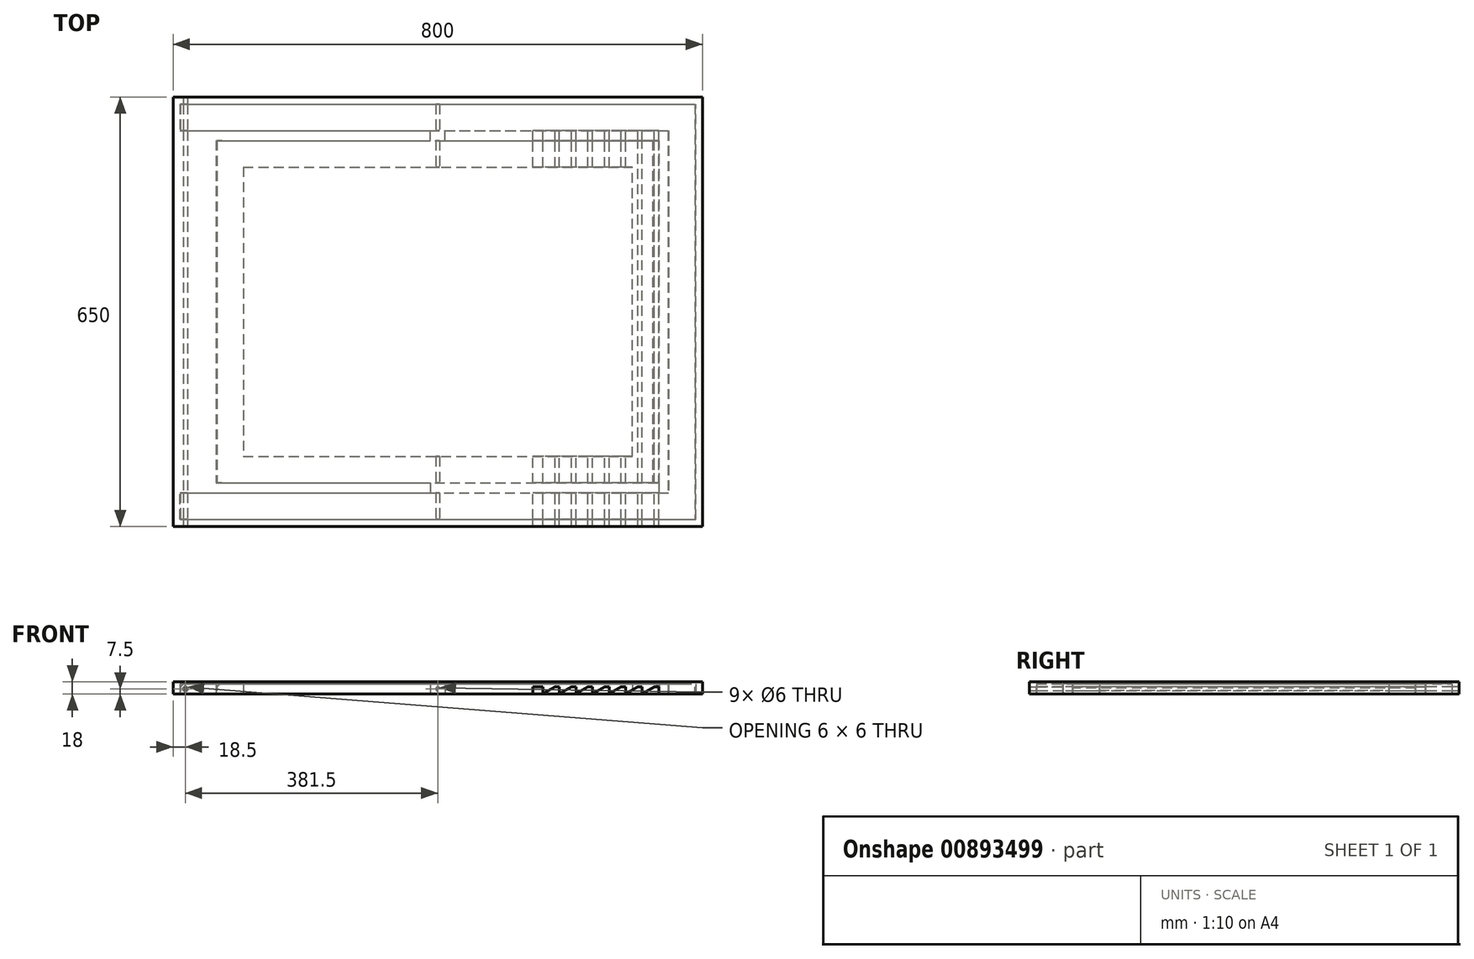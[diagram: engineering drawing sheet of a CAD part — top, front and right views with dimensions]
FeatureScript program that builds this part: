
annotation { "Feature Type Name" : "Feature", "Feature Type Description" : "" }
export const myFeature = defineFeature(function(context is Context, id is Id, definition is map)
    precondition{}
    {
        {
            assignVariable(context, id + "F0", {"name" : "leg_height", "anyValue" : 15});
        }
        {
            assignVariable(context, id + "F1", {"name" : "board_height", "anyValue" : 18});
        }
        {
            var Q0;
            Q0=qCreatedBy(makeId("Top.planeOp"),FACE);
            var sketch = newSketch(context, id + "F2", { "sketchPlane" : qUnion([Q0])});
            skLineSegment(sketch, "E0.bottom", {"start": v(400, -325) * mm, "end": v(-400, -325) * mm});
            skLineSegment(sketch, "E0.top", {"start": v(400, 325) * mm, "end": v(-400, 325) * mm});
            skLineSegment(sketch, "E0.left", {"start": v(400, -325) * mm, "end": v(400, 325) * mm});
            skLineSegment(sketch, "E0.right", {"start": v(-400, -325) * mm, "end": v(-400, 325) * mm});
            skPoint(sketch, "E0.middle", {"position": v(0, 0) * mm});
            skLineSegment(sketch, "E1", {"start": v(-389, 314) * mm, "end": v(389, 314) * mm});
            skLineSegment(sketch, "E2", {"start": v(389, 314) * mm, "end": v(389, 0) * mm});
            skLineSegment(sketch, "E3", {"start": v(-400, 0) * mm, "end": v(-334, 0) * mm, "construction": true});
            skLineSegment(sketch, "E4", {"start": v(-389, 274) * mm, "end": v(349, 274) * mm});
            skLineSegment(sketch, "E5", {"start": v(349, 274) * mm, "end": v(349, 0) * mm});
            skLineSegment(sketch, "E6", {"start": v(-389, 314) * mm, "end": v(-389, 274) * mm});
            skLineSegment(sketch, "E7", {"start": v(349, 0) * mm, "end": v(389, 0) * mm, "construction": true});
            skLineSegment(sketch, "E8", {"start": v(389, 0) * mm, "end": v(400, 0) * mm, "construction": true});
            skLineSegment(sketch, "E9", {"start": v(-334, 259) * mm, "end": v(334, 259) * mm});
            skLineSegment(sketch, "E10", {"start": v(334, 259) * mm, "end": v(334, 0) * mm});
            skLineSegment(sketch, "E11", {"start": v(-334, 259) * mm, "end": v(-334, 0) * mm});
            skLineSegment(sketch, "E12", {"start": v(-294, 0) * mm, "end": v(-294, 219) * mm});
            skLineSegment(sketch, "E13", {"start": v(-294, 219) * mm, "end": v(294, 219) * mm});
            skLineSegment(sketch, "E14", {"start": v(294, 219) * mm, "end": v(294, 0) * mm});
            skLineSegment(sketch, "E15", {"start": v(-334, 0) * mm, "end": v(-294, 0) * mm, "construction": true});
            skLineSegment(sketch, "E16", {"start": v(-294, 0) * mm, "end": v(294, 0) * mm, "construction": true});
            skLineSegment(sketch, "E17", {"start": v(294, 0) * mm, "end": v(334, 0) * mm, "construction": true});
            skLineSegment(sketch, "E18", {"start": v(334, 0) * mm, "end": v(334, 0) * mm});
            skLineSegment(sketch, "E19", {"start": v(349, 0) * mm, "end": v(349, 0) * mm});
            skLineSegment(sketch, "E20", {"start": v(334, 0) * mm, "end": v(349, 0) * mm, "construction": true});
            skLineSegment(sketch, "E21.MirrorCS", {"start": v(-294, 0) * mm, "end": v(-294, -219) * mm});
            skLineSegment(sketch, "E22.MirrorCS", {"start": v(-334, -259) * mm, "end": v(-334, 0) * mm});
            skLineSegment(sketch, "E23.MirrorCS", {"start": v(-334, -259) * mm, "end": v(334, -259) * mm});
            skLineSegment(sketch, "E24.MirrorCS", {"start": v(334, -259) * mm, "end": v(334, 0) * mm});
            skLineSegment(sketch, "E25.MirrorCS", {"start": v(294, -219) * mm, "end": v(294, 0) * mm});
            skLineSegment(sketch, "E26.MirrorCS", {"start": v(-294, -219) * mm, "end": v(294, -219) * mm});
            skLineSegment(sketch, "E27.MirrorCS", {"start": v(-389, -314) * mm, "end": v(-389, -274) * mm});
            skLineSegment(sketch, "E28.MirrorCS", {"start": v(-389, -274) * mm, "end": v(349, -274) * mm});
            skLineSegment(sketch, "E29.MirrorCS", {"start": v(-389, -314) * mm, "end": v(389, -314) * mm});
            skLineSegment(sketch, "E30.MirrorCS", {"start": v(349, -274) * mm, "end": v(349, 0) * mm});
            skLineSegment(sketch, "E31.MirrorCS", {"start": v(389, -314) * mm, "end": v(389, 0) * mm});
            skLineSegment(sketch, "E32", {"start": v(0, 325) * mm, "end": v(0, -325) * mm, "construction": true});
            skLineSegment(sketch, "E33", {"start": v(-11, 259) * mm, "end": v(-11, 274) * mm});
            skLineSegment(sketch, "E34.MirrorCS", {"start": v(11, 259) * mm, "end": v(11, 274) * mm});
            skLineSegment(sketch, "E35.MirrorCS", {"start": v(-11, -259) * mm, "end": v(-11, -274) * mm});
            skLineSegment(sketch, "E36.MirrorCS", {"start": v(11, -259) * mm, "end": v(11, -274) * mm});
            skLineSegment(sketch, "E37", {"start": v(334, -259) * mm, "end": v(334, -274) * mm});
            skLineSegment(sketch, "E38", {"start": v(334, 259) * mm, "end": v(334, 274) * mm});
            skSolve(sketch);
        }
        {
            var Q0;
            Q0 = qSketchRegion(id + "F2", true);
            var Q1;
            Q1=makeQuery(id+"F2.imprint","IMPRINT",FACE,{"disambiguationData":[TD([[makeQuery(id+"F2.imprint","IMPRINT",EDGE,{"derivedFrom":sQuery(id+"F2.wireOp",EDGE,"E1")}),-1.0]])]});
            var Q2;
            Q2=makeQuery(id+"F2.imprint","IMPRINT",FACE,{"disambiguationData":[TD([[makeQuery(id+"F2.imprint","IMPRINT",EDGE,{"derivedFrom":sQuery(id+"F2.wireOp",EDGE,"E12")}),-1.0]])]});
            var Q3;
            Q3=makeQuery(id+"F2.imprint","IMPRINT",FACE,{"disambiguationData":[TD([[makeQuery(id+"F2.imprint","IMPRINT",EDGE,{"derivedFrom":sQuery(id+"F2.wireOp",EDGE,"E9")}),-1.0]])]});
            var Q4;
            {var subQ1=sQuery(id+"F2.wireOp",EDGE,"E5");Q4=makeQuery(id+"F2.imprint","IMPRINT",FACE,{"disambiguationData":[TD([[makeQuery(id+"F2.imprint","IMPRINT",EDGE,{"derivedFrom":subQ1}),-1.0]])]});}
            var Q5;
            {var subQ0=sQuery(id+"F2.wireOp",EDGE,"E35.MirrorCS");Q5=makeQuery(id+"F2.imprint","IMPRINT",FACE,{"disambiguationData":[TD([[makeQuery(id+"F2.imprint","IMPRINT",EDGE,{"derivedFrom":subQ0}),1.0]])]});}
            var Q6;
            {var subQ0=sQuery(id+"F2.wireOp",EDGE,"E33");Q6=makeQuery(id+"F2.imprint","IMPRINT",FACE,{"disambiguationData":[TD([[makeQuery(id+"F2.imprint","IMPRINT",EDGE,{"derivedFrom":subQ0}),-1.0]])]});}
            var Q7;
            {var subQ2=sQuery(id+"F2.wireOp",EDGE,"E36.MirrorCS");Q7=makeQuery(id+"F2.imprint","IMPRINT",FACE,{"disambiguationData":[TD([[makeQuery(id+"F2.imprint","IMPRINT",EDGE,{"derivedFrom":subQ2}),1.0]])]});}
            var Q8;
            {var subQ0=sQuery(id+"F2.wireOp",EDGE,"E34.MirrorCS");Q8=makeQuery(id+"F2.imprint","IMPRINT",FACE,{"disambiguationData":[TD([[makeQuery(id+"F2.imprint","IMPRINT",EDGE,{"derivedFrom":subQ0}),-1.0]])]});}
            extrude(context, id + "F3", {"entities" : qUnion([Q0, Q1, Q2, Q3, Q4, Q5, Q6, Q7, Q8]), "depth" : (getVariable(context, 'board_height')) * mm, "offsetDistance" : 25 * mm});
        }
        {
            var Q0;
            Q0=makeQuery(id+"F2.imprint","IMPRINT",FACE,{"disambiguationData":[TD([[makeQuery(id+"F2.imprint","IMPRINT",EDGE,{"derivedFrom":sQuery(id+"F2.wireOp",EDGE,"E9")}),-1.0]])]});
            var Q1;
            Q1=makeQuery(id+"F2.imprint","IMPRINT",FACE,{"disambiguationData":[TD([[makeQuery(id+"F2.imprint","IMPRINT",EDGE,{"derivedFrom":sQuery(id+"F2.wireOp",EDGE,"E1")}),-1.0]])]});
            extrude(context, id + "F4", {"entities" : qUnion([Q0, Q1]), "depth" : (getVariable(context, 'leg_height')) * mm, "offsetDistance" : 25 * mm});
        }
        {
            var Q0;
            Q0=makeQuery(id+"F4.opExtrude","SWEPT_BODY",BODY,{"disambiguationData":[OSD([sQuery(id+"F2.wireOp",EDGE,"E1"),sQuery(id+"F2.wireOp",EDGE,"E2"),sQuery(id+"F2.wireOp",EDGE,"E4"),sQuery(id+"F2.wireOp",EDGE,"E5"),sQuery(id+"F2.wireOp",EDGE,"E6"),sQuery(id+"F2.wireOp",EDGE,"E27.MirrorCS"),sQuery(id+"F2.wireOp",EDGE,"E28.MirrorCS"),sQuery(id+"F2.wireOp",EDGE,"E29.MirrorCS"),sQuery(id+"F2.wireOp",EDGE,"E30.MirrorCS"),sQuery(id+"F2.wireOp",EDGE,"E31.MirrorCS")])]});
            var Q1;
            Q1=makeQuery(id+"F4.opExtrude","SWEPT_BODY",BODY,{"disambiguationData":[OSD([sQuery(id+"F2.wireOp",EDGE,"E9"),sQuery(id+"F2.wireOp",EDGE,"E10"),sQuery(id+"F2.wireOp",EDGE,"E11"),sQuery(id+"F2.wireOp",EDGE,"E12"),sQuery(id+"F2.wireOp",EDGE,"E13"),sQuery(id+"F2.wireOp",EDGE,"E14"),sQuery(id+"F2.wireOp",EDGE,"E21.MirrorCS"),sQuery(id+"F2.wireOp",EDGE,"E22.MirrorCS"),sQuery(id+"F2.wireOp",EDGE,"E23.MirrorCS"),sQuery(id+"F2.wireOp",EDGE,"E24.MirrorCS"),sQuery(id+"F2.wireOp",EDGE,"E25.MirrorCS"),sQuery(id+"F2.wireOp",EDGE,"E26.MirrorCS")])]});
            var Q2;
            Q2=makeQuery(id+"F3.opExtrude","SWEPT_BODY",BODY,{"disambiguationData":[OSD([sQuery(id+"F2.wireOp",EDGE,"E0.bottom"),sQuery(id+"F2.wireOp",EDGE,"E0.top"),sQuery(id+"F2.wireOp",EDGE,"E0.left"),sQuery(id+"F2.wireOp",EDGE,"E0.right")])]});
            var Q3;
            Q3=makeQuery(id+"F4.opExtrude","SWEPT_FACE",FACE,{"disambiguationData":[OSD([sQuery(id+"F2.wireOp",EDGE,"E2"),sQuery(id+"F2.wireOp",EDGE,"E31.MirrorCS")])]});
            var Q4;
            Q4=makeQuery(id+"F4.opExtrude","SWEPT_FACE",FACE,{"disambiguationData":[OSD([sQuery(id+"F2.wireOp",EDGE,"E5"),sQuery(id+"F2.wireOp",EDGE,"E30.MirrorCS")])]});
            var Q5;
            Q5=makeQuery(id+"F4.opExtrude","SWEPT_FACE",FACE,{"disambiguationData":[OSD([sQuery(id+"F2.wireOp",EDGE,"E14"),sQuery(id+"F2.wireOp",EDGE,"E25.MirrorCS")])]});
            var Q6;
            Q6=makeQuery(id+"F4.opExtrude","SWEPT_FACE",FACE,{"disambiguationData":[OSD([sQuery(id+"F2.wireOp",EDGE,"E10"),sQuery(id+"F2.wireOp",EDGE,"E24.MirrorCS")])]});
            var Q7;
            Q7=makeQuery(id+"F4.opExtrude","SWEPT_FACE",FACE,{"disambiguationData":[OSD([sQuery(id+"F2.wireOp",EDGE,"E11"),sQuery(id+"F2.wireOp",EDGE,"E22.MirrorCS")])]});
            var Q8;
            Q8=makeQuery(id+"F4.opExtrude","SWEPT_FACE",FACE,{"disambiguationData":[OSD([sQuery(id+"F2.wireOp",EDGE,"E12"),sQuery(id+"F2.wireOp",EDGE,"E21.MirrorCS")])]});
            var Q9;
            Q9=makeQuery(id+"F4.opExtrude","SWEPT_FACE",FACE,{"disambiguationData":[OSD([sQuery(id+"F2.wireOp",EDGE,"E6")])]});
            var Q10;
            Q10=makeQuery(id+"F4.opExtrude","SWEPT_FACE",FACE,{"disambiguationData":[OSD([sQuery(id+"F2.wireOp",EDGE,"E27.MirrorCS")])]});
            booleanBodies(context, id + "F5", {"operationType" : BooleanOperationType.SUBTRACTION, "tools" : qUnion([Q0, Q1]), "targets" : qUnion([Q2]), "offset" : true, "entitiesToOffset" : qUnion([Q3, Q4, Q5, Q6, Q7, Q8, Q9, Q10]), "offsetDistance" : 1 * mm, "keepTools" : true});
        }
        {
            var Q0;
            Q0=makeQuery(id+"F4.opExtrude","CAP_EDGE",EDGE,{"disambiguationData":[OSD([sQuery(id+"F2.wireOp",EDGE,"E27.MirrorCS")])],"isStart":true});
            var Q1;
            Q1=makeQuery(id+"F4.opExtrude","CAP_EDGE",EDGE,{"disambiguationData":[OSD([sQuery(id+"F2.wireOp",EDGE,"E27.MirrorCS")])],"isStart":false});
            var Q2;
            Q2=makeQuery(id+"F4.opExtrude","CAP_EDGE",EDGE,{"disambiguationData":[OSD([sQuery(id+"F2.wireOp",EDGE,"E6")])],"isStart":true});
            var Q3;
            Q3=makeQuery(id+"F4.opExtrude","CAP_EDGE",EDGE,{"disambiguationData":[OSD([sQuery(id+"F2.wireOp",EDGE,"E6")])],"isStart":false});
            var Q4;
            Q4=makeQuery(id+"F4.opExtrude","CAP_EDGE",EDGE,{"disambiguationData":[OSD([sQuery(id+"F2.wireOp",EDGE,"E11"),sQuery(id+"F2.wireOp",EDGE,"E22.MirrorCS")])],"isStart":true});
            var Q5;
            Q5=makeQuery(id+"F4.opExtrude","CAP_EDGE",EDGE,{"disambiguationData":[OSD([sQuery(id+"F2.wireOp",EDGE,"E11"),sQuery(id+"F2.wireOp",EDGE,"E22.MirrorCS")])],"isStart":false});
            var Q6;
            Q6=makeQuery(id+"F4.opExtrude","CAP_EDGE",EDGE,{"disambiguationData":[OSD([sQuery(id+"F2.wireOp",EDGE,"E10"),sQuery(id+"F2.wireOp",EDGE,"E24.MirrorCS")])],"isStart":false});
            var Q7;
            Q7=makeQuery(id+"F4.opExtrude","CAP_EDGE",EDGE,{"disambiguationData":[OSD([sQuery(id+"F2.wireOp",EDGE,"E2"),sQuery(id+"F2.wireOp",EDGE,"E31.MirrorCS")])],"isStart":false});
            var Q8;
            Q8=makeQuery(id+"F4.opExtrude","CAP_EDGE",EDGE,{"disambiguationData":[OSD([sQuery(id+"F2.wireOp",EDGE,"E2"),sQuery(id+"F2.wireOp",EDGE,"E31.MirrorCS")])],"isStart":true});
            var Q9;
            Q9=makeQuery(id+"F4.opExtrude","CAP_EDGE",EDGE,{"disambiguationData":[OSD([sQuery(id+"F2.wireOp",EDGE,"E10"),sQuery(id+"F2.wireOp",EDGE,"E24.MirrorCS")])],"isStart":true});
            fillet(context, id + "F6", {"entities" : qUnion([Q0, Q1, Q2, Q3, Q4, Q5, Q6, Q7, Q8, Q9]), "radius" : (getVariable(context, 'leg_height') / 2) * mm, "tangentPropagation" : true, "allowEdgeOverflow" : false});
        }
        {
            var Q0;
            {var subQ0=sQuery(id+"F2.wireOp",EDGE,"E35.MirrorCS");Q0=makeQuery(id+"F2.imprint","IMPRINT",FACE,{"disambiguationData":[TD([[makeQuery(id+"F2.imprint","IMPRINT",EDGE,{"derivedFrom":subQ0}),1.0]])]});}
            var Q1;
            {var subQ0=sQuery(id+"F2.wireOp",EDGE,"E33");Q1=makeQuery(id+"F2.imprint","IMPRINT",FACE,{"disambiguationData":[TD([[makeQuery(id+"F2.imprint","IMPRINT",EDGE,{"derivedFrom":subQ0}),-1.0]])]});}
            var Q2;
            Q2=makeQuery(id+"F2.imprint","IMPRINT",FACE,{"disambiguationData":[TD([[makeQuery(id+"F2.imprint","IMPRINT",EDGE,{"derivedFrom":sQuery(id+"F2.wireOp",EDGE,"E12")}),-1.0]])]});
            var Q3;
            {var subQ2=sQuery(id+"F2.wireOp",EDGE,"E36.MirrorCS");Q3=makeQuery(id+"F2.imprint","IMPRINT",FACE,{"disambiguationData":[TD([[makeQuery(id+"F2.imprint","IMPRINT",EDGE,{"derivedFrom":subQ2}),1.0]])]});}
            var Q4;
            {var subQ0=sQuery(id+"F2.wireOp",EDGE,"E34.MirrorCS");Q4=makeQuery(id+"F2.imprint","IMPRINT",FACE,{"disambiguationData":[TD([[makeQuery(id+"F2.imprint","IMPRINT",EDGE,{"derivedFrom":subQ0}),-1.0]])]});}
            extrude(context, id + "F7", {"entities" : qUnion([Q0, Q1, Q2, Q3, Q4]), "operationType" : NewBodyOperationType.REMOVE, "depth" : (getVariable(context, 'leg_height')) * mm, "offsetDistance" : 25 * mm});
        }
        {
            var Q0;
            Q0=makeQuery(id+"F3.opExtrude","SWEPT_FACE",FACE,{"disambiguationData":[OSD([sQuery(id+"F2.wireOp",EDGE,"E0.bottom")])]});
            var sketch = newSketch(context, id + "F8", { "sketchPlane" : qUnion([Q0])});
            skPoint(sketch, "E39", {"position": v(-381.5, 7.5) * mm});
            skPoint(sketch, "E40", {"position": v(0, 7.5) * mm});
            skPoint(sketch, "E41", {"position": v(326.5, 7.5) * mm});
            skSolve(sketch);
        }
        {
            var Q0;
            Q0=sQuery(id+"F8.wireOp",VERTEX,"E39");
            var Q1;
            Q1=makeQuery(id+"F3.opExtrude","SWEPT_BODY",BODY,{"disambiguationData":[OSD([sQuery(id+"F2.wireOp",EDGE,"E0.bottom"),sQuery(id+"F2.wireOp",EDGE,"E0.top"),sQuery(id+"F2.wireOp",EDGE,"E0.left"),sQuery(id+"F2.wireOp",EDGE,"E0.right")])]});
            var Q2;
            Q2=makeQuery(id+"F4.opExtrude","SWEPT_BODY",BODY,{"disambiguationData":[OSD([sQuery(id+"F2.wireOp",EDGE,"E1"),sQuery(id+"F2.wireOp",EDGE,"E2"),sQuery(id+"F2.wireOp",EDGE,"E4"),sQuery(id+"F2.wireOp",EDGE,"E5"),sQuery(id+"F2.wireOp",EDGE,"E6"),sQuery(id+"F2.wireOp",EDGE,"E27.MirrorCS"),sQuery(id+"F2.wireOp",EDGE,"E28.MirrorCS"),sQuery(id+"F2.wireOp",EDGE,"E29.MirrorCS"),sQuery(id+"F2.wireOp",EDGE,"E30.MirrorCS"),sQuery(id+"F2.wireOp",EDGE,"E31.MirrorCS")])]});
            hole(context, id + "F9", {"style" : HoleStyle.SIMPLE, "endStyle" : HoleEndStyle.THROUGH, "holeDiameter" : 6 * mm, "majorDiameter" : 5 * mm, "isTappedThrough" : true, "tappedDepth" : 12 * mm, "tapClearance" : 3, "locations" : qUnion([Q0]), "scope" : qUnion([Q1, Q2])});
        }
        {
            var Q0;
            Q0=sQuery(id+"F8.wireOp",VERTEX,"E40");
            var Q1;
            Q1=makeQuery(id+"F4.opExtrude","SWEPT_BODY",BODY,{"disambiguationData":[OSD([sQuery(id+"F2.wireOp",EDGE,"E1"),sQuery(id+"F2.wireOp",EDGE,"E2"),sQuery(id+"F2.wireOp",EDGE,"E4"),sQuery(id+"F2.wireOp",EDGE,"E5"),sQuery(id+"F2.wireOp",EDGE,"E6"),sQuery(id+"F2.wireOp",EDGE,"E27.MirrorCS"),sQuery(id+"F2.wireOp",EDGE,"E28.MirrorCS"),sQuery(id+"F2.wireOp",EDGE,"E29.MirrorCS"),sQuery(id+"F2.wireOp",EDGE,"E30.MirrorCS"),sQuery(id+"F2.wireOp",EDGE,"E31.MirrorCS")])]});
            var Q2;
            Q2=makeQuery(id+"F4.opExtrude","SWEPT_BODY",BODY,{"disambiguationData":[OSD([sQuery(id+"F2.wireOp",EDGE,"E9"),sQuery(id+"F2.wireOp",EDGE,"E10"),sQuery(id+"F2.wireOp",EDGE,"E11"),sQuery(id+"F2.wireOp",EDGE,"E12"),sQuery(id+"F2.wireOp",EDGE,"E13"),sQuery(id+"F2.wireOp",EDGE,"E14"),sQuery(id+"F2.wireOp",EDGE,"E21.MirrorCS"),sQuery(id+"F2.wireOp",EDGE,"E22.MirrorCS"),sQuery(id+"F2.wireOp",EDGE,"E23.MirrorCS"),sQuery(id+"F2.wireOp",EDGE,"E24.MirrorCS"),sQuery(id+"F2.wireOp",EDGE,"E25.MirrorCS"),sQuery(id+"F2.wireOp",EDGE,"E26.MirrorCS")])]});
            hole(context, id + "F10", {"style" : HoleStyle.SIMPLE, "endStyle" : HoleEndStyle.THROUGH, "holeDiameter" : 6 * mm, "majorDiameter" : 5 * mm, "isTappedThrough" : true, "tappedDepth" : 12 * mm, "tapClearance" : 3, "locations" : qUnion([Q0]), "scope" : qUnion([Q1, Q2])});
        }
        {
            var Q0;
            Q0=sQuery(id+"F8.wireOp",VERTEX,"E41");
            var Q1;
            Q1=makeQuery(id+"F4.opExtrude","SWEPT_BODY",BODY,{"disambiguationData":[OSD([sQuery(id+"F2.wireOp",EDGE,"E9"),sQuery(id+"F2.wireOp",EDGE,"E10"),sQuery(id+"F2.wireOp",EDGE,"E11"),sQuery(id+"F2.wireOp",EDGE,"E12"),sQuery(id+"F2.wireOp",EDGE,"E13"),sQuery(id+"F2.wireOp",EDGE,"E14"),sQuery(id+"F2.wireOp",EDGE,"E21.MirrorCS"),sQuery(id+"F2.wireOp",EDGE,"E22.MirrorCS"),sQuery(id+"F2.wireOp",EDGE,"E23.MirrorCS"),sQuery(id+"F2.wireOp",EDGE,"E24.MirrorCS"),sQuery(id+"F2.wireOp",EDGE,"E25.MirrorCS"),sQuery(id+"F2.wireOp",EDGE,"E26.MirrorCS")])]});
            hole(context, id + "F11", {"style" : HoleStyle.SIMPLE, "endStyle" : HoleEndStyle.THROUGH, "holeDiameter" : 5 * mm, "majorDiameter" : 5 * mm, "isTappedThrough" : true, "tappedDepth" : 12 * mm, "tapClearance" : 3, "locations" : qUnion([Q0]), "scope" : qUnion([Q1])});
        }
        {
            var Q0;
            {var subQ0=sQuery(id+"F2.wireOp",EDGE,"E34.MirrorCS");Q0=makeQuery(id+"F2.imprint","IMPRINT",FACE,{"disambiguationData":[TD([[makeQuery(id+"F2.imprint","IMPRINT",EDGE,{"derivedFrom":subQ0}),-1.0]])]});}
            extrude(context, id + "F12", {"entities" : qUnion([Q0]), "depth" : (getVariable(context, 'leg_height')) * mm, "offsetDistance" : 25 * mm});
        }
        {
            var Q0;
            Q0=makeQuery(id+"F12.opExtrude","SWEPT_FACE",FACE,{"disambiguationData":[OSD([sQuery(id+"F2.wireOp",EDGE,"E4")])]});
            var sketch = newSketch(context, id + "F13", { "sketchPlane" : qUnion([Q0])});
            skLineSegment(sketch, "E42", {"start": v(-334, 10.5) * mm, "end": v(-327.19, 10.5) * mm});
            skLineSegment(sketch, "E43", {"start": v(-327.19, 10.5) * mm, "end": v(-310.5, 0.87) * mm});
            skLineSegment(sketch, "E44", {"start": v(-309, 1.73) * mm, "end": v(-309, 10.5) * mm});
            skPoint(sketch, "E45.visualSharp", {"position": v(-309, 0) * mm});
            skArc(sketch, "E45.filletArc", {"start": v(-310.5, 0.87) * mm, "mid": v(-309.5, 0.87) * mm, "end": v(-309, 1.73) * mm});
            skLineSegment(sketch, "E46.1.0.0", {"start": v(-309, 10.5) * mm, "end": v(-302.19, 10.5) * mm});
            skLineSegment(sketch, "E46.1.0.1", {"start": v(-302.19, 10.5) * mm, "end": v(-285.5, 0.87) * mm});
            skLineSegment(sketch, "E46.1.0.2", {"start": v(-284, 1.73) * mm, "end": v(-284, 10.5) * mm});
            skArc(sketch, "E46.1.0.3", {"start": v(-285.5, 0.87) * mm, "mid": v(-284.5, 0.87) * mm, "end": v(-284, 1.73) * mm});
            skLineSegment(sketch, "E46.2.0.0", {"start": v(-284, 10.5) * mm, "end": v(-277.19, 10.5) * mm});
            skLineSegment(sketch, "E46.2.0.1", {"start": v(-277.19, 10.5) * mm, "end": v(-260.5, 0.87) * mm});
            skLineSegment(sketch, "E46.2.0.2", {"start": v(-259, 1.73) * mm, "end": v(-259, 10.5) * mm});
            skArc(sketch, "E46.2.0.3", {"start": v(-260.5, 0.87) * mm, "mid": v(-259.5, 0.87) * mm, "end": v(-259, 1.73) * mm});
            skLineSegment(sketch, "E46.direction1", {"start": v(-334, 10.5) * mm, "end": v(-309, 10.5) * mm, "construction": true});
            skLineSegment(sketch, "E47.0.3.0", {"start": v(-259, 10.5) * mm, "end": v(-252.19, 10.5) * mm});
            skLineSegment(sketch, "E47.3.3.0", {"start": v(-252.19, 10.5) * mm, "end": v(-235.5, 0.87) * mm});
            skLineSegment(sketch, "E47.6.3.0", {"start": v(-234, 1.73) * mm, "end": v(-234, 10.5) * mm});
            skArc(sketch, "E47.9.3.0", {"start": v(-235.5, 0.87) * mm, "mid": v(-234.5, 0.87) * mm, "end": v(-234, 1.73) * mm});
            skLineSegment(sketch, "E47.0.4.0", {"start": v(-234, 10.5) * mm, "end": v(-227.19, 10.5) * mm});
            skLineSegment(sketch, "E47.3.4.0", {"start": v(-227.19, 10.5) * mm, "end": v(-210.5, 0.87) * mm});
            skLineSegment(sketch, "E47.6.4.0", {"start": v(-209, 1.73) * mm, "end": v(-209, 10.5) * mm});
            skArc(sketch, "E47.9.4.0", {"start": v(-210.5, 0.87) * mm, "mid": v(-209.5, 0.87) * mm, "end": v(-209, 1.73) * mm});
            skLineSegment(sketch, "E47.0.5.0", {"start": v(-209, 10.5) * mm, "end": v(-202.19, 10.5) * mm});
            skLineSegment(sketch, "E47.3.5.0", {"start": v(-202.19, 10.5) * mm, "end": v(-185.5, 0.87) * mm});
            skLineSegment(sketch, "E47.6.5.0", {"start": v(-184, 1.73) * mm, "end": v(-184, 10.5) * mm});
            skArc(sketch, "E47.9.5.0", {"start": v(-185.5, 0.87) * mm, "mid": v(-184.5, 0.87) * mm, "end": v(-184, 1.73) * mm});
            skLineSegment(sketch, "E47.0.6.0", {"start": v(-184, 10.5) * mm, "end": v(-177.19, 10.5) * mm});
            skLineSegment(sketch, "E47.3.6.0", {"start": v(-177.19, 10.5) * mm, "end": v(-160.5, 0.87) * mm});
            skLineSegment(sketch, "E47.6.6.0", {"start": v(-159, 1.73) * mm, "end": v(-159, 10.5) * mm});
            skArc(sketch, "E47.9.6.0", {"start": v(-160.5, 0.87) * mm, "mid": v(-159.5, 0.87) * mm, "end": v(-159, 1.73) * mm});
            skLineSegment(sketch, "E48", {"start": v(-144, 0) * mm, "end": v(-334, 0) * mm});
            skLineSegment(sketch, "E49", {"start": v(-334, 0) * mm, "end": v(-334, 10.5) * mm});
            skLineSegment(sketch, "E50", {"start": v(-144, 10.5) * mm, "end": v(-144, 0) * mm});
            skLineSegment(sketch, "E51", {"start": v(-159, 10.5) * mm, "end": v(-144, 10.5) * mm});
            skSolve(sketch);
        }
        {
            var Q0;
            Q0=makeQuery(id+"F13.imprint","IMPRINT",FACE,{"disambiguationData":[TD([[makeQuery(id+"F13.imprint","IMPRINT",EDGE,{"derivedFrom":sQuery(id+"F13.wireOp",EDGE,"E42")}),-1.0]])]});
            extrude(context, id + "F14", {"entities" : qUnion([Q0]), "operationType" : NewBodyOperationType.REMOVE, "endBound" : BoundingType.THROUGH_ALL, "oppositeDirection" : true, "depth" : 25 * mm, "offsetDistance" : 25 * mm});
        }
    });
